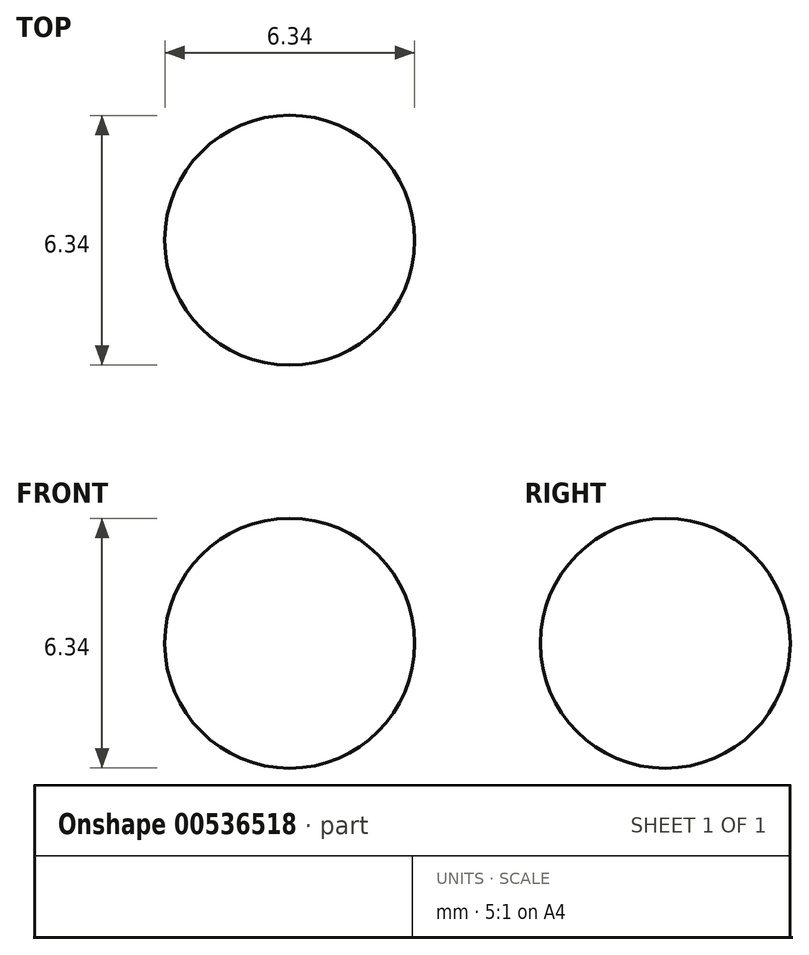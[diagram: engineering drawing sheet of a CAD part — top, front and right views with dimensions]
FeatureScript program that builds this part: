
annotation { "Feature Type Name" : "Feature", "Feature Type Description" : "" }
export const myFeature = defineFeature(function(context is Context, id is Id, definition is map)
    precondition{}
    {
        {
            var Q0;
            Q0=qCreatedBy(makeId("Top.planeOp"),FACE);
            var sketch = newSketch(context, id + "F0", { "sketchPlane" : qUnion([Q0])});
            skLineSegment(sketch, "E0", {"start": v(0, -3.17) * mm, "end": v(0, 3.18) * mm});
            skArc(sketch, "E1", {"start": v(0, -3.18) * mm, "mid": v(3.18, 0) * mm, "end": v(0, 3.18) * mm});
            skSolve(sketch);
        }
        {
            var Q0;
            Q0 = qSketchRegion(id + "F0", true);
            var Q1;
            Q1=sQuery(id+"F0.wireOp",EDGE,"E0");
            revolve(context, id + "F1", {"entities" : qUnion([Q0]), "axis" : qUnion([Q1]), "revolveType" : RevolveType.FULL});
        }
    });
